# Revit family: ADSK_Конвектор электрический_KH-1
name_source: partatom
category: Оборудование
units: mm (PartAtom-declared; Revit-internal decimal feet)

## family parameters
Всегда вертикально = Да
На основе рабочей плоскости = Нет
Общий = Нет
При загрузке вырезать с полостями = Нет
Размер круглого соединителя = Использовать диаметр
Тип детали = Нормальный
Точка расчета площади = Нет

## types (3) — shared parameters
ADSK_URL документации изделия = http://kalashnikov-climate.com
ADSK_URL страницы изделия = https://tizest.ru
ADSK_Единица измерения = шт.
ADSK_Завод-изготовитель = ООО "ИЗТТ"
ADSK_Классификация нагрузок = Прочее
ADSK_Количество = 1
ADSK_Количество фаз = 1
ADSK_Количество фаз числовое = 1
ADSK_Масса = 4
ADSK_Материал наименование = Серый
ADSK_Напряжение = 230 В
URL = https://tizest.ru
Высота = 215 мм
Глубина = 120 мм
Материал корпуса = Белый
Материал креплений = Черный

## per-type parameters (varying)
| type | ADSK_Коэффициент мощности | ADSK_Наименование | ADSK_Номинальная мощность | ADSK_Полная мощность | ADSK_Тепловая мощность | ADSK_Ток | Ширина |
| KH-E025M-54 | 0.494071 | Конвектор электрический, степень защиты IP54, 250 Вт | 250 Вт | 506 В·А | 250 Вт | 2 А | 570 мм |
| KH-E075M-54 | 0.741107 | Конвектор электрический, степень защиты IP54, 750 Вт | 750 Вт | 1012 В·А | 750 Вт | 4 А | 705 мм |
| KH-E100M-54 | 0.66379 | Конвектор электрический, степень защиты IP54, 1000 Вт | 1000 Вт | 1507 В·А | 1000 Вт | 7 А | 940 мм |

note: column(s) folded — value = type name in every type: ADSK_Код изделия, ADSK_Марка

## geometry (parser evidence)
native form markers: Blend x2
no freeform markers — native parametric forms only
